# Revit family: Grohe_ConcealedShowerSystemWithRainshowerSmartActive310_34863KF0
name_source: partatom
category: Plumbing Fixtures
units: mm (PartAtom-declared; Revit-internal decimal feet)

## family parameters
Cut with Voids When Loaded = No
Host = Face
OmniClass Number = 23.45.05.00
OmniClass Title = Sanitary Equipment
Part Type = Normal
Room Calculation Point = No
Round Connector Dimension = Use Diameter
Shared = No

## types (1)
- Concealed Shower System With Rainshower SmartActive 310 (34863KF0)
    Assembly Code = D2013
    AssetType = Fixed
    BIMObjectName = Grohe_ConcealedShowerSystemWithRainshowerSmartActive310_34863KF0
    CO2NeutralProduction = GROHE is one of the first leading manufacturer within the sanitary industry having a CO2-neutral production.
    ClassificationName = Uniclass2015
    ClassificationValue = Pr_40_20_87_55
    Color = Grohe_Black
    Cost = 0 $
    Default Elevation = 0 mm  [stored 0 ft]
    Description = Concealed Shower System With Rainshower SmartActive 310
    DimensionsDocumentLink = https://cdn.cloud.grohe.com
    DocumentationCertificates = https://www.bimstore.co
    DocumentationInstallationGuide = https://www.bimstore.co
    DocumentationLiterature = https://www.bimstore.co
    DocumentationMaintenance = https://www.bimstore.co
    DocumentationTechnical = https://www.bimstore.co
    DurationUnit = Years
    EF000007 = true
    EF000008 = true
    EF000010 = true
    EF000040 = true
    EF000113 = true
    EF000301 = true
    EF000303 = true
    EF000329 = true
    EF000332 = true
    EF000634 = true
    EF000664 = true
    EF001187 = true
    EF001438 = true
    EF001707 = true
    EF002149 = true
    EF002594 = true
    EF002671 = true
    EF003454 = true
    EF003829 = true
    EF005084 = true
    EF005474 = true
    EF005545 = true
    EF005870 = true
    EF006485 = true
    EF006569 = true
    EF006974 = true
    EF008277 = true
    EF010904 = true
    EF011622 = true
    EF011625 = true
    EF011626 = true
    EF011779 = true
    EF012491 = true
    EF012637 = true
    EF013621 = true
    EF014578 = true
    EF015359 = true
    EF016731 = true
    EF020075 = Yes
    EF020348 = true
    EF020779 = true
    EF020780 = true
    EF020784 = true
    EF020785 = true
    EF020787 = true
    EF020789 = true
    EF020790 = true
    EF020792 = true
    EF020794 = true
    EF020797 = true
    EF020798 = true
    EF020799 = true
    EF020801 = true
    EF020803 = true
    EF020825 = true
    EF020826 = true
    EF020873 = true
    EF020990 = true
    EF021035 = true
    EF021038 = true
    EF021039 = true
    EF021040 = true
    EF021607 = true
    EF021652 = true
    EF021758 = true
    EF021760 = true
    EF021835 = true
    EF022116 = true
    EF022168 = true
    EF022182 = true
    EF022222 = true
    EF022223 = true
    EF022225 = true
    EF022252 = true
    EF022267 = true
    EF022268 = true
    EF022269 = true
    EF022338 = true
    EF022377 = true
    EF022393 = true
    EF022394 = true
    EF022398 = true
    EF022750 = true
    EF023452 = true
    EF023686 = true
    EF023688 = true
    EF023790 = true
    EF023957 = true
    EF024051 = true
    EF024078 = true
    EF024225 = true
    EF024471 = true
    EF024474 = true
    EF024492 = true
    EF024494 = true
    EF024495 = true
    EF024552 = true
    EF024736 = true
    EF024897 = true
    EF024922 = true
    EF025080 = true
    EF025093 = true
    EF025101 = true
    EF025104 = true
    EF025107 = true
    EF025247 = true
    EF025336 = true
    EFNL0001 = true
    Ecojoy = No
    ExpectedLife = 0
    Finish = Black
    FullRecyclabilityOfPlastic = All plastic components are fully recycable
    GROHESocialCommittment = green.grohe.com/social_engagement
    GROHESustainability = green.grohe.com
    IfcExportAs = IfcPipeFitting
    IfcExportType = IfcPipeFittingType
    Keynote = N16
    Manufacturer = Grohe
    ManufacturerName = Grohe
    Model = Concealed Shower System With Rainshower SmartActive 310
    ModelNumber = 34863KF0
    ModelReference = Concealed Shower System With Rainshower SmartActive 310
    NBSDescription = Shower fittings package
    NBSObjectName = Grohe - Shower fittings package
    NBSReference = 45-35-70/325
    NominalDepth = 0 mm  [stored 0 ft]
    NominalHeight = 0 mm  [stored 0 ft]
    NominalLength = 0 mm  [stored 0 ft]
    PrimaryMaterial = Grohe_Black
    ProductDescription = consisting of:

concealed thermostat with 3 valves

GROHE Rapido SmartBox universal rough-in box, 1/2" (35 604)

Rainshower SmartActive 310 head shower set 2 sprays including horizontal shower arm 430 mm and head shower rough-in (26 483)

Rainshower SmartActive 130 hand shower 3 sprays

shower outlet elbow 1/2" with holder

Silverflex shower hose 1500 mm 1/2" x 1/2"

optional flow regulator 9.5 l/min included for hand shower
    ProductNumber = 34863KF0
    ProductShortText = Concealed shower system with Rainshower SmartActive 310
    ProductType = Thermostat
    ProductionYear = 2023
    SustainabilityAward = green.grohe.com/awards
    SustainabilityReport = green.grohe.com/reporting
    Type Comments = Concealed Shower System With Rainshower SmartActive 310
    TypeName = Concealed Shower System With Rainshower SmartActive 310
    URL = https://www.grohe.co.uk
    WarrantyDurationLabor = 0
    WarrantyDurationParts = 0
    WarrantyDurationUnit = Years
    _BSBibleVersion = 17
    _BimSpecGuid = 0
    _CurrentRevision = 1
    _DistributedBy = https://www.bimstore.co
    _ObjectUserGuide = https://www.bimstore.co

note: [stored X ft] marks values corroborated as IEEE doubles in the binary element streams (Revit-internal decimal feet)

## geometry (parser evidence)
native form markers: Sweep x1
no freeform markers — native parametric forms only
